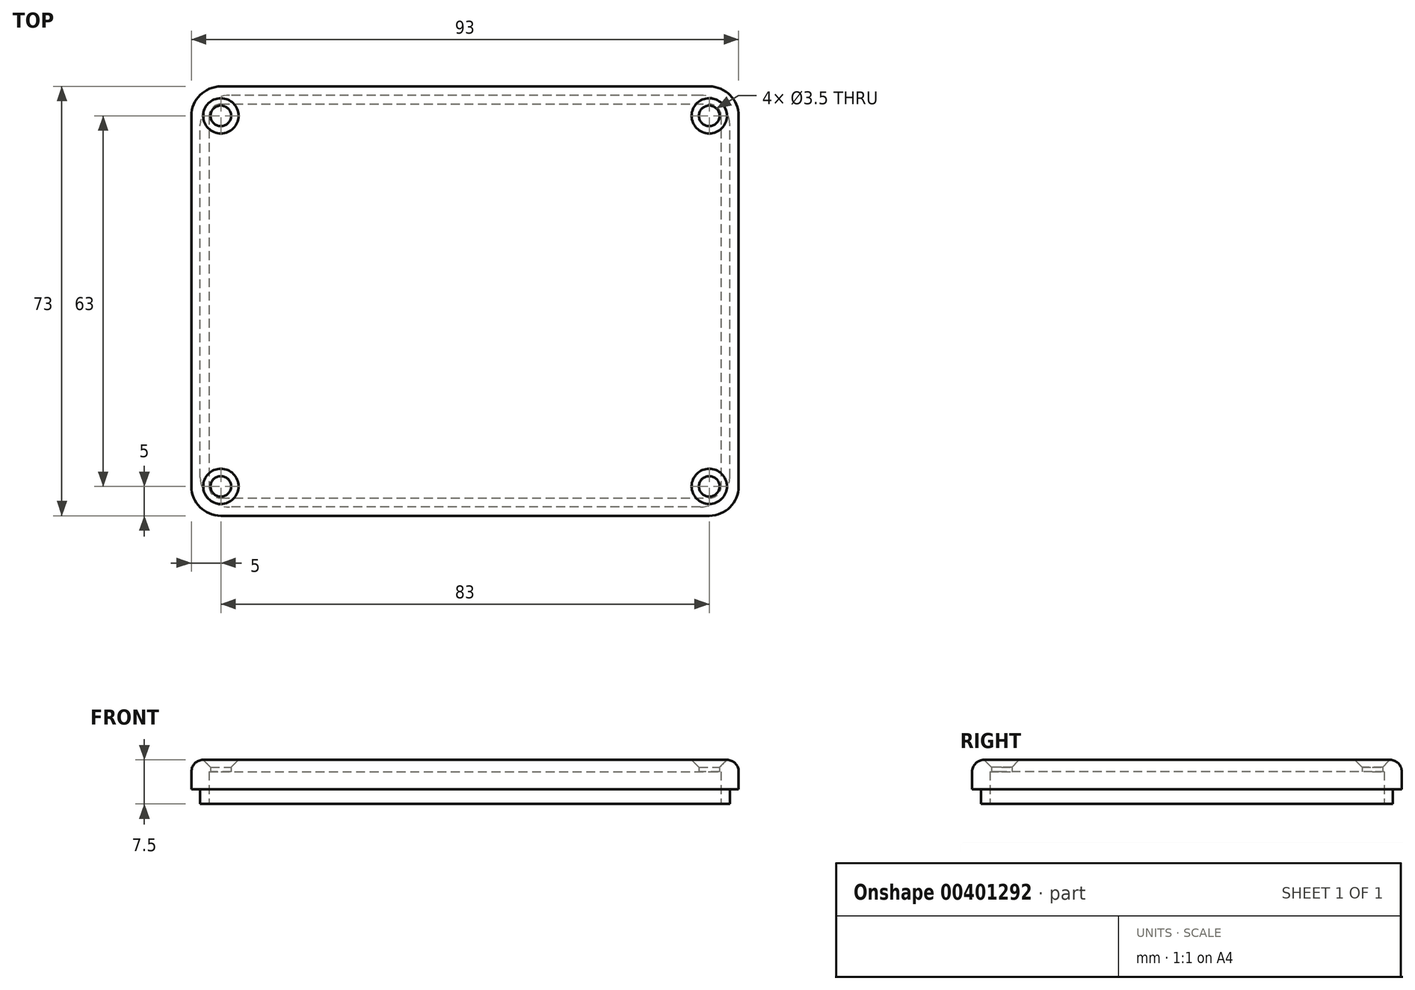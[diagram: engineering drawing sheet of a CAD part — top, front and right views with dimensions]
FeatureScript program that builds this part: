
annotation { "Feature Type Name" : "Feature", "Feature Type Description" : "" }
export const myFeature = defineFeature(function(context is Context, id is Id, definition is map)
    precondition{}
    {
        {
            var Q0;
            Q0=qCreatedBy(makeId("Top.planeOp"),FACE);
            var sketch = newSketch(context, id + "F0", { "sketchPlane" : qUnion([Q0])});
            skLineSegment(sketch, "E0.bottom", {"start": v(45, -35) * mm, "end": v(-45, -35) * mm});
            skLineSegment(sketch, "E0.top", {"start": v(45, 35) * mm, "end": v(-45, 35) * mm});
            skLineSegment(sketch, "E0.left", {"start": v(45, -35) * mm, "end": v(45, 35) * mm});
            skLineSegment(sketch, "E0.right", {"start": v(-45, -35) * mm, "end": v(-45, 35) * mm});
            skLineSegment(sketch, "E1.bottom", {"start": v(-46.5, 36.5) * mm, "end": v(46.5, 36.5) * mm});
            skLineSegment(sketch, "E1.top", {"start": v(-46.5, -36.5) * mm, "end": v(46.5, -36.5) * mm});
            skLineSegment(sketch, "E1.left", {"start": v(-46.5, 36.5) * mm, "end": v(-46.5, -36.5) * mm});
            skLineSegment(sketch, "E1.right", {"start": v(46.5, 36.5) * mm, "end": v(46.5, -36.5) * mm});
            skLineSegment(sketch, "E2", {"start": v(-74.18, 0) * mm, "end": v(81.2, 0) * mm, "construction": true});
            skPoint(sketch, "E3", {"position": v(45, 0) * mm});
            skLineSegment(sketch, "E4.bottom", {"start": v(-43.5, 33.5) * mm, "end": v(43.5, 33.5) * mm});
            skLineSegment(sketch, "E4.top", {"start": v(-43.5, -33.5) * mm, "end": v(43.5, -33.5) * mm});
            skLineSegment(sketch, "E4.left", {"start": v(-43.5, 33.5) * mm, "end": v(-43.5, -33.5) * mm});
            skLineSegment(sketch, "E4.right", {"start": v(43.5, 33.5) * mm, "end": v(43.5, -33.5) * mm});
            skPoint(sketch, "E4.middle", {"position": v(0, 0) * mm});
            skPoint(sketch, "E5", {"position": v(0, 36.5) * mm});
            skPoint(sketch, "E6", {"position": v(-41.5, 31.5) * mm});
            skPoint(sketch, "E7.MirrorP", {"position": v(-41.5, -31.5) * mm});
            skPoint(sketch, "E8.MirrorP", {"position": v(41.5, -31.5) * mm});
            skPoint(sketch, "E9.MirrorP", {"position": v(41.5, 31.5) * mm});
            skSolve(sketch);
        }
        {
            var Q0;
            Q0=makeQuery(id+"F0.imprint","IMPRINT",FACE,{"disambiguationData":[TD([[makeQuery(id+"F0.imprint","IMPRINT",EDGE,{"derivedFrom":sQuery(id+"F0.wireOp",EDGE,"8c8745d5-5b30-4063-88c9-152bd3a8d934")}),-1.0]])]});
            var Q1;
            Q1=makeQuery(id+"F0.imprint","IMPRINT",FACE,{"disambiguationData":[TD([[makeQuery(id+"F0.imprint","IMPRINT",EDGE,{"derivedFrom":sQuery(id+"F0.wireOp",EDGE,"E0.bottom")}),-1.0]])]});
            var Q2;
            Q2=makeQuery(id+"F0.imprint","IMPRINT",FACE,{"disambiguationData":[TD([[makeQuery(id+"F0.imprint","IMPRINT",EDGE,{"derivedFrom":sQuery(id+"F0.wireOp",EDGE,"E0.bottom")}),1.0]])]});
            var Q3;
            Q3=makeQuery(id+"F0.imprint","IMPRINT",FACE,{"disambiguationData":[TD([[makeQuery(id+"F0.imprint","IMPRINT",EDGE,{"derivedFrom":sQuery(id+"F0.wireOp",EDGE,"E4.bottom")}),-1.0]])]});
            extrude(context, id + "F1", {"entities" : qUnion([Q0, Q1, Q2, Q3]), "depth" : 5 * mm});
        }
        {
            var Q0;
            Q0=makeQuery(id+"F0.imprint","IMPRINT",FACE,{"disambiguationData":[TD([[makeQuery(id+"F0.imprint","IMPRINT",EDGE,{"derivedFrom":sQuery(id+"F0.wireOp",EDGE,"8c8745d5-5b30-4063-88c9-152bd3a8d934")}),-1.0]])]});
            var Q1;
            Q1=makeQuery(id+"F0.imprint","IMPRINT",FACE,{"disambiguationData":[TD([[makeQuery(id+"F0.imprint","IMPRINT",EDGE,{"derivedFrom":sQuery(id+"F0.wireOp",EDGE,"E4.bottom")}),-1.0]])]});
            extrude(context, id + "F2", {"entities" : qUnion([Q0, Q1]), "operationType" : NewBodyOperationType.REMOVE, "depth" : 3 * mm});
        }
        {
            var Q0;
            Q0=makeQuery(id+"F0.imprint","IMPRINT",FACE,{"disambiguationData":[TD([[makeQuery(id+"F0.imprint","IMPRINT",EDGE,{"derivedFrom":sQuery(id+"F0.wireOp",EDGE,"E0.bottom")}),-1.0]])]});
            extrude(context, id + "F3", {"entities" : qUnion([Q0]), "operationType" : NewBodyOperationType.ADD, "oppositeDirection" : true, "depth" : 2.5 * mm});
        }
        {
            var Q0;
            {var subQ0=sQuery(id+"F0.wireOp",EDGE,"E4.left");var subQ1=sQuery(id+"F0.wireOp",EDGE,"E4.top");Q0=makeQuery(id+"F3.boolean.opBoolean","MERGE",EDGE,{"derivedFrom":[makeQuery(id+"F2.boolean.opBoolean","COPY",EDGE,{"derivedFrom":makeQuery(id+"F2.opExtrude","SWEPT_EDGE",EDGE,{"disambiguationData":[OSD([subQ1,subQ0])]})}),makeQuery(id+"F3.opExtrude","SWEPT_EDGE",EDGE,{"disambiguationData":[OSD([subQ1,subQ0])]})]});}
            var Q1;
            {var subQ0=sQuery(id+"F0.wireOp",EDGE,"E4.left");var subQ1=sQuery(id+"F0.wireOp",EDGE,"E4.bottom");Q1=makeQuery(id+"F3.boolean.opBoolean","MERGE",EDGE,{"derivedFrom":[makeQuery(id+"F2.boolean.opBoolean","COPY",EDGE,{"derivedFrom":makeQuery(id+"F2.opExtrude","SWEPT_EDGE",EDGE,{"disambiguationData":[OSD([subQ1,subQ0])]})}),makeQuery(id+"F3.opExtrude","SWEPT_EDGE",EDGE,{"disambiguationData":[OSD([subQ1,subQ0])]})]});}
            var Q2;
            {var subQ0=sQuery(id+"F0.wireOp",EDGE,"E4.right");var subQ1=sQuery(id+"F0.wireOp",EDGE,"E4.bottom");Q2=makeQuery(id+"F3.boolean.opBoolean","MERGE",EDGE,{"derivedFrom":[makeQuery(id+"F2.boolean.opBoolean","COPY",EDGE,{"derivedFrom":makeQuery(id+"F2.opExtrude","SWEPT_EDGE",EDGE,{"disambiguationData":[OSD([subQ1,subQ0])]})}),makeQuery(id+"F3.opExtrude","SWEPT_EDGE",EDGE,{"disambiguationData":[OSD([subQ1,subQ0])]})]});}
            var Q3;
            {var subQ0=sQuery(id+"F0.wireOp",EDGE,"E4.right");var subQ1=sQuery(id+"F0.wireOp",EDGE,"E4.top");Q3=makeQuery(id+"F3.boolean.opBoolean","MERGE",EDGE,{"derivedFrom":[makeQuery(id+"F2.boolean.opBoolean","COPY",EDGE,{"derivedFrom":makeQuery(id+"F2.opExtrude","SWEPT_EDGE",EDGE,{"disambiguationData":[OSD([subQ1,subQ0])]})}),makeQuery(id+"F3.opExtrude","SWEPT_EDGE",EDGE,{"disambiguationData":[OSD([subQ1,subQ0])]})]});}
            var Q4;
            Q4=makeQuery(id+"F1.opExtrude","CAP_EDGE",EDGE,{"disambiguationData":[OSD([sQuery(id+"F0.wireOp",EDGE,"E1.top")])],"isStart":false});
            var Q5;
            Q5=makeQuery(id+"F1.opExtrude","CAP_EDGE",EDGE,{"disambiguationData":[OSD([sQuery(id+"F0.wireOp",EDGE,"E1.right")])],"isStart":false});
            var Q6;
            Q6=makeQuery(id+"F1.opExtrude","CAP_EDGE",EDGE,{"disambiguationData":[OSD([sQuery(id+"F0.wireOp",EDGE,"E1.left")])],"isStart":false});
            var Q7;
            Q7=makeQuery(id+"F1.opExtrude","CAP_EDGE",EDGE,{"disambiguationData":[OSD([sQuery(id+"F0.wireOp",EDGE,"E1.bottom")])],"isStart":false});
            fillet(context, id + "F4", {"entities" : qUnion([Q0, Q1, Q2, Q3, Q4, Q5, Q6, Q7]), "radius" : 2 * mm, "tangentPropagation" : true, "allowEdgeOverflow" : false});
        }
        {
            var Q0;
            Q0=makeQuery(id+"F3.opExtrude","SWEPT_EDGE",EDGE,{"disambiguationData":[OSD([sQuery(id+"F0.wireOp",EDGE,"E0.bottom"),sQuery(id+"F0.wireOp",EDGE,"E0.right")])]});
            var Q1;
            Q1=makeQuery(id+"F1.opExtrude","SWEPT_EDGE",EDGE,{"disambiguationData":[OSD([sQuery(id+"F0.wireOp",EDGE,"E1.top"),sQuery(id+"F0.wireOp",EDGE,"E1.left")])]});
            var Q2;
            Q2=makeQuery(id+"F1.opExtrude","SWEPT_EDGE",EDGE,{"disambiguationData":[OSD([sQuery(id+"F0.wireOp",EDGE,"E1.top"),sQuery(id+"F0.wireOp",EDGE,"E1.right")])]});
            var Q3;
            Q3=makeQuery(id+"F3.opExtrude","SWEPT_EDGE",EDGE,{"disambiguationData":[OSD([sQuery(id+"F0.wireOp",EDGE,"E0.bottom"),sQuery(id+"F0.wireOp",EDGE,"E0.left")])]});
            var Q4;
            Q4=makeQuery(id+"F1.opExtrude","SWEPT_EDGE",EDGE,{"disambiguationData":[OSD([sQuery(id+"F0.wireOp",EDGE,"E1.bottom"),sQuery(id+"F0.wireOp",EDGE,"E1.right")])]});
            var Q5;
            Q5=makeQuery(id+"F3.opExtrude","SWEPT_EDGE",EDGE,{"disambiguationData":[OSD([sQuery(id+"F0.wireOp",EDGE,"E0.top"),sQuery(id+"F0.wireOp",EDGE,"E0.left")])]});
            var Q6;
            Q6=makeQuery(id+"F1.opExtrude","SWEPT_EDGE",EDGE,{"disambiguationData":[OSD([sQuery(id+"F0.wireOp",EDGE,"E1.bottom"),sQuery(id+"F0.wireOp",EDGE,"E1.left")])]});
            var Q7;
            Q7=makeQuery(id+"F3.opExtrude","SWEPT_EDGE",EDGE,{"disambiguationData":[OSD([sQuery(id+"F0.wireOp",EDGE,"E0.top"),sQuery(id+"F0.wireOp",EDGE,"E0.right")])]});
            fillet(context, id + "F5", {"entities" : qUnion([Q0, Q1, Q2, Q3, Q4, Q5, Q6, Q7]), "radius" : 5 * mm, "tangentPropagation" : true, "allowEdgeOverflow" : false});
        }
        {
            var Q0;
            Q0=makeQuery(id+"F1.opExtrude","CAP_FACE",FACE,{"disambiguationData":[OSD([sQuery(id+"F0.wireOp",EDGE,"E1.bottom"),sQuery(id+"F0.wireOp",EDGE,"E1.top"),sQuery(id+"F0.wireOp",EDGE,"E1.left"),sQuery(id+"F0.wireOp",EDGE,"E1.right")])],"isStart":false});
            var sketch = newSketch(context, id + "F6", { "sketchPlane" : qUnion([Q0])});
            skPoint(sketch, "E10", {"position": v(41.5, -31.5) * mm});
            skPoint(sketch, "E11", {"position": v(-41.5, -31.5) * mm});
            skPoint(sketch, "E12", {"position": v(-41.5, 31.5) * mm});
            skPoint(sketch, "E13", {"position": v(41.5, 31.5) * mm});
            skSolve(sketch);
        }
        {
            var Q0;
            Q0=sQuery(id+"F6.wireOp",VERTEX,"E10");
            var Q1;
            Q1=sQuery(id+"F6.wireOp",VERTEX,"E11");
            var Q2;
            Q2=sQuery(id+"F6.wireOp",VERTEX,"E12");
            var Q3;
            Q3=sQuery(id+"F6.wireOp",VERTEX,"E13");
            var Q4;
            Q4=makeQuery(id+"F1.opExtrude","SWEPT_BODY",BODY,{"disambiguationData":[OSD([sQuery(id+"F0.wireOp",EDGE,"E1.bottom"),sQuery(id+"F0.wireOp",EDGE,"E1.top"),sQuery(id+"F0.wireOp",EDGE,"E1.left"),sQuery(id+"F0.wireOp",EDGE,"E1.right")])]});
            hole(context, id + "F7", {"style" : HoleStyle.C_SINK, "endStyle" : HoleEndStyle.BLIND, "holeDiameter" : 3.5 * mm, "cSinkDiameter" : 6 * mm, "cSinkAngle" : 90 * degree, "holeDepth" : 6 * mm, "isTappedThrough" : true, "tappedDepth" : 12 * mm, "tapClearance" : 3, "locations" : qUnion([Q0, Q1, Q2, Q3]), "scope" : qUnion([Q4]), "startStyle" : HoleStartStyle.SKETCH});
        }
    });
